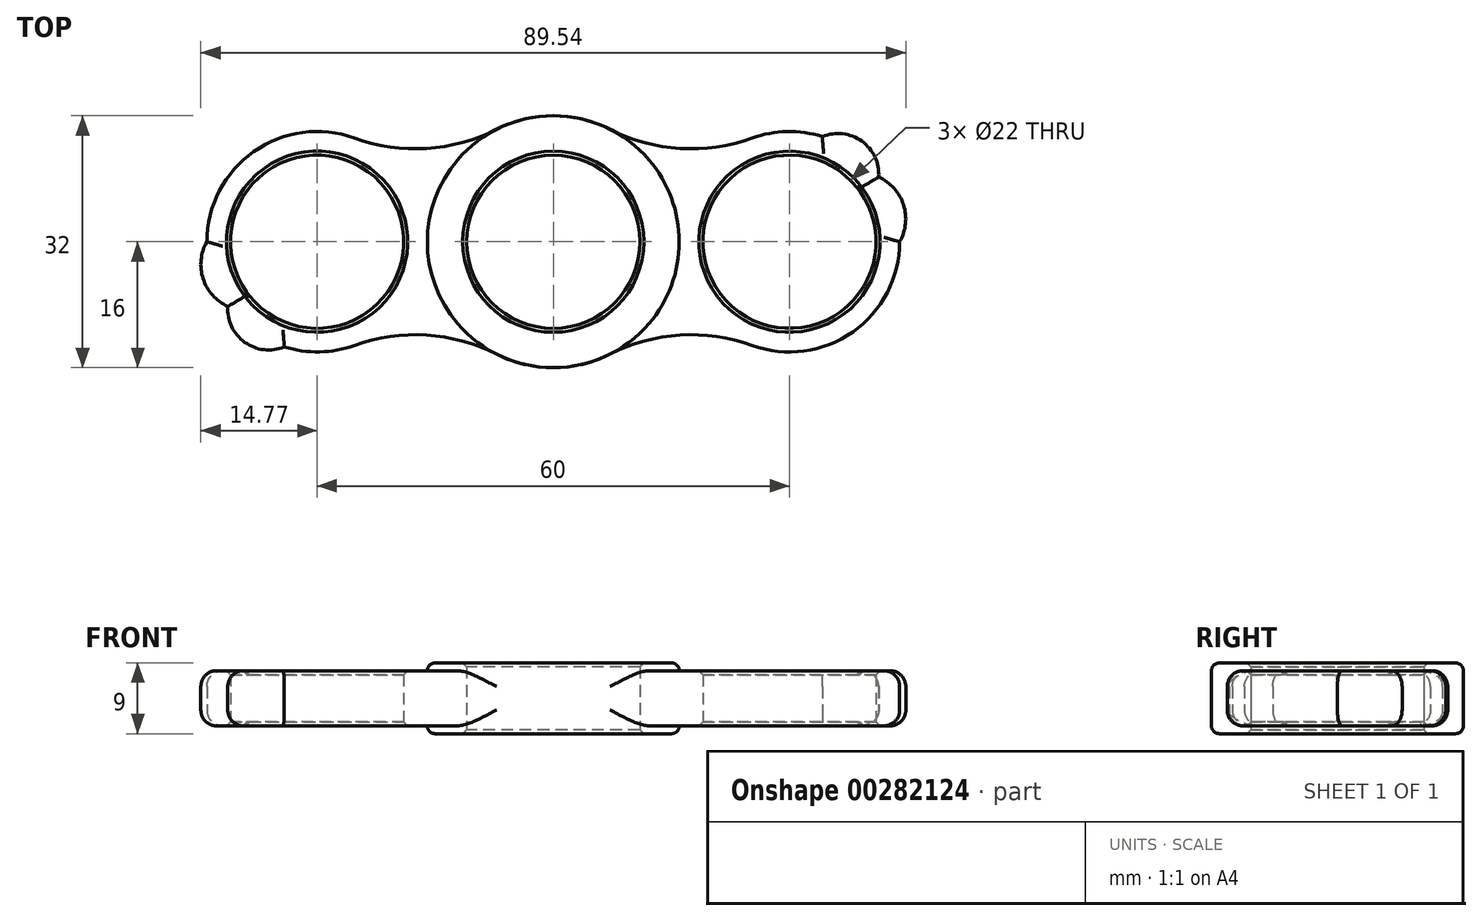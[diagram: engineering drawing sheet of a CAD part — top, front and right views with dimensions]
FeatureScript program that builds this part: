
annotation { "Feature Type Name" : "Feature", "Feature Type Description" : "" }
export const myFeature = defineFeature(function(context is Context, id is Id, definition is map)
    precondition{}
    {
        {
            var Q0;
            Q0=qCreatedBy(makeId("Top.planeOp"),FACE);
            var sketch = newSketch(context, id + "F0", { "sketchPlane" : qUnion([Q0])});
            skCircle(sketch, "E0", {"center": v(0, 0) * mm, "radius": 11 * mm});
            skCircle(sketch, "E1", {"center": v(0, 0) * mm, "radius": 16 * mm});
            skLineSegment(sketch, "E2", {"start": v(0, 0) * mm, "end": v(22, 0) * mm, "construction": true});
            skLineSegment(sketch, "E3", {"start": v(0, 0) * mm, "end": v(30, 0) * mm, "construction": true});
            skCircle(sketch, "E4", {"center": v(30, 0) * mm, "radius": 11 * mm});
            skCircle(sketch, "E5", {"center": v(30, 0) * mm, "radius": 14 * mm});
            skArc(sketch, "E6", {"start": v(34.92, 19.9) * mm, "mid": v(16.33, 11.85) * mm, "end": v(-1.32, 21.8) * mm});
            skArc(sketch, "E7.MirrorCS", {"start": v(34.92, -19.9) * mm, "mid": v(16.33, -11.85) * mm, "end": v(-1.32, -21.8) * mm});
            skArc(sketch, "E8", {"start": v(41.34, 8.21) * mm, "mid": v(39.2, 12.77) * mm, "end": v(34.19, 13.36) * mm});
            skArc(sketch, "E9", {"start": v(44, 0) * mm, "mid": v(44.49, 4.7) * mm, "end": v(41.34, 8.21) * mm});
            skArc(sketch, "E10.MirrorCS", {"start": v(41.34, -8.21) * mm, "mid": v(39.2, -12.77) * mm, "end": v(34.19, -13.36) * mm});
            skArc(sketch, "E11.MirrorCS", {"start": v(44, 0) * mm, "mid": v(44.49, -4.7) * mm, "end": v(41.34, -8.21) * mm});
            skSolve(sketch);
        }
        {
            var Q0;
            Q0=makeQuery(id+"F0.imprint","IMPRINT",FACE,{"disambiguationData":[TD([[makeQuery(id+"F0.imprint","IMPRINT",EDGE,{"derivedFrom":sQuery(id+"F0.wireOp",EDGE,"E0")}),-1.0]])]});
            extrude(context, id + "F1", {"entities" : qUnion([Q0]), "endBound" : BoundingType.SYMMETRIC, "depth" : 9 * mm});
        }
        {
            var Q0;
            {var subQ0=sQuery(id+"F0.wireOp",EDGE,"E6");var subQ1=sQuery(id+"F0.wireOp",EDGE,"E1");var subQ2=makeQuery(id+"F0.imprint","INTERSECT",VERTEX,{"derivedFrom":[subQ1,subQ0]});Q0=makeQuery(id+"F0.imprint","IMPRINT",FACE,{"disambiguationData":[TD([[makeQuery(id+"F0.imprint","IMPRINT",EDGE,{"disambiguationData":[TD([[subQ2,1.0]])],"derivedFrom":subQ1}),-1.0]])]});}
            var Q1;
            Q1=makeQuery(id+"F0.imprint","IMPRINT",FACE,{"disambiguationData":[TD([[makeQuery(id+"F0.imprint","IMPRINT",EDGE,{"derivedFrom":sQuery(id+"F0.wireOp",EDGE,"E4")}),-1.0]])]});
            var Q2;
            {var subQ0=sQuery(id+"F0.wireOp",EDGE,"gSAZEsJJ-cn3l-cjJ6-9HDa-52uPBN5IA6vx");Q2=makeQuery(id+"F0.imprint","IMPRINT",FACE,{"disambiguationData":[TD([[makeQuery(id+"F0.imprint","IMPRINT",EDGE,{"derivedFrom":subQ0}),1.0]])]});}
            var Q3;
            {var subQ0=sQuery(id+"F0.wireOp",EDGE,"E8");Q3=makeQuery(id+"F0.imprint","IMPRINT",FACE,{"disambiguationData":[TD([[makeQuery(id+"F0.imprint","IMPRINT",EDGE,{"derivedFrom":subQ0}),1.0]])]});}
            var Q4;
            {var subQ0=sQuery(id+"F0.wireOp",EDGE,"f63044cd-322f-4f96-b824-94d15fe920c80.MirrorCS");Q4=makeQuery(id+"F0.imprint","IMPRINT",FACE,{"disambiguationData":[TD([[makeQuery(id+"F0.imprint","IMPRINT",EDGE,{"derivedFrom":subQ0}),-1.0]])]});}
            var Q5;
            {var subQ0=sQuery(id+"F0.wireOp",EDGE,"E10.MirrorCS");Q5=makeQuery(id+"F0.imprint","IMPRINT",FACE,{"disambiguationData":[TD([[makeQuery(id+"F0.imprint","IMPRINT",EDGE,{"derivedFrom":subQ0}),-1.0]])]});}
            var Q6;
            {var subQ0=sQuery(id+"F0.wireOp",EDGE,"E11.MirrorCS");Q6=makeQuery(id+"F0.imprint","IMPRINT",FACE,{"disambiguationData":[TD([[makeQuery(id+"F0.imprint","IMPRINT",EDGE,{"derivedFrom":subQ0}),-1.0]])]});}
            var Q7;
            {var subQ0=sQuery(id+"F0.wireOp",EDGE,"E9");Q7=makeQuery(id+"F0.imprint","IMPRINT",FACE,{"disambiguationData":[TD([[makeQuery(id+"F0.imprint","IMPRINT",EDGE,{"derivedFrom":subQ0}),1.0]])]});}
            var Q8;
            {var subQ0=sQuery(id+"F0.wireOp",EDGE,"E7.MirrorCS");var subQ1=sQuery(id+"F0.wireOp",EDGE,"E1");var subQ2=makeQuery(id+"F0.imprint","INTERSECT",VERTEX,{"derivedFrom":[subQ1,subQ0]});Q8=makeQuery(id+"F0.imprint","IMPRINT",FACE,{"disambiguationData":[TD([[makeQuery(id+"F0.imprint","IMPRINT",EDGE,{"disambiguationData":[TD([[subQ2,-1.0]])],"derivedFrom":subQ1}),-1.0]])]});}
            extrude(context, id + "F2", {"entities" : qUnion([Q0, Q1, Q2, Q3, Q4, Q5, Q6, Q7, Q8]), "operationType" : NewBodyOperationType.ADD, "endBound" : BoundingType.SYMMETRIC, "depth" : 7 * mm});
        }
        {
            var Q0;
            Q0=makeQuery(id+"F2.opExtrude","CAP_EDGE",EDGE,{"disambiguationData":[OSD([sQuery(id+"F0.wireOp",EDGE,"E6")])],"isStart":false});
            var Q1;
            Q1=makeQuery(id+"F2.opExtrude","CAP_EDGE",EDGE,{"disambiguationData":[OSD([sQuery(id+"F0.wireOp",EDGE,"gSAZEsJJ-cn3l-cjJ6-9HDa-52uPBN5IA6vx")])],"isStart":false});
            var Q2;
            Q2=makeQuery(id+"F2.opExtrude","CAP_EDGE",EDGE,{"disambiguationData":[OSD([sQuery(id+"F0.wireOp",EDGE,"E8")])],"isStart":false});
            var Q3;
            Q3=makeQuery(id+"F2.opExtrude","CAP_EDGE",EDGE,{"disambiguationData":[OSD([sQuery(id+"F0.wireOp",EDGE,"E9")])],"isStart":false});
            var Q4;
            Q4=makeQuery(id+"F2.opExtrude","CAP_EDGE",EDGE,{"disambiguationData":[OSD([sQuery(id+"F0.wireOp",EDGE,"E11.MirrorCS")])],"isStart":false});
            var Q5;
            Q5=makeQuery(id+"F2.opExtrude","CAP_EDGE",EDGE,{"disambiguationData":[OSD([sQuery(id+"F0.wireOp",EDGE,"E10.MirrorCS")])],"isStart":false});
            var Q6;
            Q6=makeQuery(id+"F2.opExtrude","CAP_EDGE",EDGE,{"disambiguationData":[OSD([sQuery(id+"F0.wireOp",EDGE,"f63044cd-322f-4f96-b824-94d15fe920c80.MirrorCS")])],"isStart":false});
            var Q7;
            Q7=makeQuery(id+"F2.opExtrude","CAP_EDGE",EDGE,{"disambiguationData":[OSD([sQuery(id+"F0.wireOp",EDGE,"E7.MirrorCS")])],"isStart":false});
            var Q8;
            Q8=makeQuery(id+"F2.opExtrude","CAP_EDGE",EDGE,{"disambiguationData":[OSD([sQuery(id+"F0.wireOp",EDGE,"E6")])],"isStart":true});
            var Q9;
            Q9=makeQuery(id+"F2.opExtrude","CAP_EDGE",EDGE,{"disambiguationData":[OSD([sQuery(id+"F0.wireOp",EDGE,"E7.MirrorCS")])],"isStart":true});
            var Q10;
            Q10=makeQuery(id+"F2.opExtrude","CAP_EDGE",EDGE,{"disambiguationData":[OSD([sQuery(id+"F0.wireOp",EDGE,"gSAZEsJJ-cn3l-cjJ6-9HDa-52uPBN5IA6vx")])],"isStart":true});
            var Q11;
            Q11=makeQuery(id+"F2.opExtrude","CAP_EDGE",EDGE,{"disambiguationData":[OSD([sQuery(id+"F0.wireOp",EDGE,"E8")])],"isStart":true});
            var Q12;
            Q12=makeQuery(id+"F2.opExtrude","CAP_EDGE",EDGE,{"disambiguationData":[OSD([sQuery(id+"F0.wireOp",EDGE,"E9")])],"isStart":true});
            var Q13;
            Q13=makeQuery(id+"F2.opExtrude","CAP_EDGE",EDGE,{"disambiguationData":[OSD([sQuery(id+"F0.wireOp",EDGE,"E11.MirrorCS")])],"isStart":true});
            var Q14;
            Q14=makeQuery(id+"F2.opExtrude","CAP_EDGE",EDGE,{"disambiguationData":[OSD([sQuery(id+"F0.wireOp",EDGE,"E10.MirrorCS")])],"isStart":true});
            var Q15;
            Q15=makeQuery(id+"F2.opExtrude","CAP_EDGE",EDGE,{"disambiguationData":[OSD([sQuery(id+"F0.wireOp",EDGE,"f63044cd-322f-4f96-b824-94d15fe920c80.MirrorCS")])],"isStart":true});
            fillet(context, id + "F3", {"entities" : qUnion([Q0, Q1, Q2, Q3, Q4, Q5, Q6, Q7, Q8, Q9, Q10, Q11, Q12, Q13, Q14, Q15]), "radius" : 2 * mm, "tangentPropagation" : true, "allowEdgeOverflow" : false});
        }
        {
            var Q0;
            Q0=makeQuery(id+"F1.opExtrude","CAP_EDGE",EDGE,{"disambiguationData":[OSD([sQuery(id+"F0.wireOp",EDGE,"E1")])],"isStart":true});
            var Q1;
            Q1=makeQuery(id+"F1.opExtrude","CAP_EDGE",EDGE,{"disambiguationData":[OSD([sQuery(id+"F0.wireOp",EDGE,"E1")])],"isStart":false});
            fillet(context, id + "F4", {"entities" : qUnion([Q0, Q1]), "radius" : 1 * mm, "tangentPropagation" : true, "allowEdgeOverflow" : false});
        }
        {
            var Q0;
            Q0=makeQuery(id+"F1.opExtrude","SWEPT_FACE",FACE,{"disambiguationData":[OSD([sQuery(id+"F0.wireOp",EDGE,"E0")])]});
            var Q1;
            Q1=makeQuery(id+"F2.opExtrude","SWEPT_FACE",FACE,{"disambiguationData":[OSD([sQuery(id+"F0.wireOp",EDGE,"E4")])]});
            chamfer(context, id + "F5", {"entities" : qUnion([Q0, Q1]), "width" : .5 * mm, "tangentPropagation" : true});
        }
        {
            var Q0;
            Q0=makeQuery(id+"F1.opExtrude","SWEPT_BODY",BODY,{"disambiguationData":[OSD([sQuery(id+"F0.wireOp",EDGE,"E0"),sQuery(id+"F0.wireOp",EDGE,"E1"),sQuery(id+"F0.wireOp",EDGE,"E4"),sQuery(id+"F0.wireOp",EDGE,"E6"),sQuery(id+"F0.wireOp",EDGE,"E7.MirrorCS"),sQuery(id+"F0.wireOp",EDGE,"gSAZEsJJ-cn3l-cjJ6-9HDa-52uPBN5IA6vx"),sQuery(id+"F0.wireOp",EDGE,"E8"),sQuery(id+"F0.wireOp",EDGE,"E9"),sQuery(id+"F0.wireOp",EDGE,"f63044cd-322f-4f96-b824-94d15fe920c80.MirrorCS"),sQuery(id+"F0.wireOp",EDGE,"E10.MirrorCS"),sQuery(id+"F0.wireOp",EDGE,"E11.MirrorCS")])]});
            var Q1;
            Q1=makeQuery(id+"F1.opExtrude","SWEPT_FACE",FACE,{"disambiguationData":[OSD([sQuery(id+"F0.wireOp",EDGE,"E0")])]});
            circularPattern(context, id + "F6", {"operationType" : NewBodyOperationType.ADD, "entities" : qUnion([Q0]), "axis" : qUnion([Q1]), "angle" : 360 * degree, "instanceCount" : 2, "equalSpace" : true});
        }
    });
